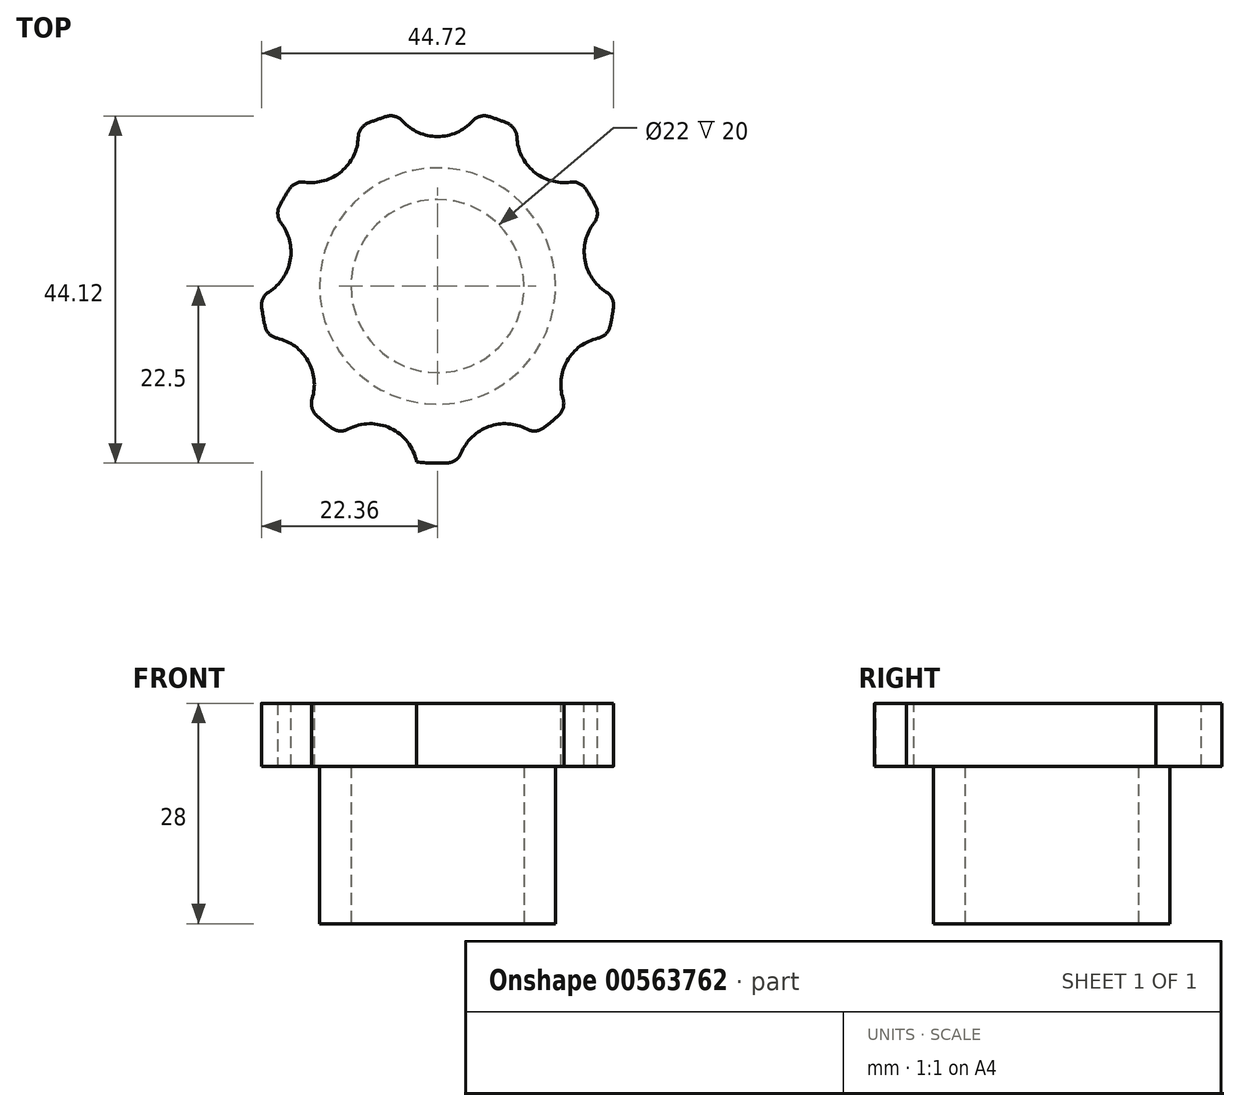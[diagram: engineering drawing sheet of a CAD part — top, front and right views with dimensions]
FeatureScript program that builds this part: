
annotation { "Feature Type Name" : "Feature", "Feature Type Description" : "" }
export const myFeature = defineFeature(function(context is Context, id is Id, definition is map)
    precondition{}
    {
        {
            var Q0;
            Q0=qCreatedBy(makeId("Top.planeOp"),FACE);
            var sketch = newSketch(context, id + "F0", { "sketchPlane" : qUnion([Q0])});
            skCircle(sketch, "E0", {"center": v(0, 0) * mm, "radius": 11 * mm});
            skCircle(sketch, "E1", {"center": v(0, 0) * mm, "radius": 15 * mm});
            skSolve(sketch);
        }
        {
            var Q0;
            Q0=makeQuery(id+"F0.imprint","IMPRINT",FACE,{"disambiguationData":[TD([[makeQuery(id+"F0.imprint","IMPRINT",EDGE,{"derivedFrom":sQuery(id+"F0.wireOp",EDGE,"E0")}),-1.0]])]});
            extrude(context, id + "F1", {"entities" : qUnion([Q0]), "depth" : 20 * mm, "offsetDistance" : 25 * mm});
        }
        {
            var Q0;
            Q0=makeQuery(id+"F1.opExtrude","CAP_FACE",FACE,{"disambiguationData":[OSD([sQuery(id+"F0.wireOp",EDGE,"E0"),sQuery(id+"F0.wireOp",EDGE,"E1")])],"isStart":false});
            var sketch = newSketch(context, id + "F2", { "sketchPlane" : qUnion([Q0])});
            skCircle(sketch, "E2", {"center": v(0, 0) * mm, "radius": 22.5 * mm});
            skSolve(sketch);
        }
        {
            var Q0;
            Q0 = qSketchRegion(id + "F2", true);
            extrude(context, id + "F3", {"entities" : qUnion([Q0]), "operationType" : NewBodyOperationType.ADD, "depth" : 8 * mm, "offsetDistance" : 25 * mm});
        }
        {
            var Q0;
            Q0=makeQuery(id+"F3.opExtrude","CAP_FACE",FACE,{"disambiguationData":[OSD([sQuery(id+"F2.wireOp",EDGE,"E2")])],"isStart":false});
            var sketch = newSketch(context, id + "F4", { "sketchPlane" : qUnion([Q0])});
            skCircle(sketch, "E3", {"center": v(0, 25) * mm, "radius": 6 * mm});
            skCircle(sketch, "E4.1.0", {"center": v(-16.07, 19.15) * mm, "radius": 6 * mm});
            skCircle(sketch, "E4.2.0", {"center": v(-24.62, 4.34) * mm, "radius": 6 * mm});
            skCircle(sketch, "E4.3.0", {"center": v(-21.65, -12.5) * mm, "radius": 6 * mm});
            skCircle(sketch, "E4.4.0", {"center": v(-8.55, -23.5) * mm, "radius": 6 * mm});
            skCircle(sketch, "E4.5.0", {"center": v(8.55, -23.5) * mm, "radius": 6 * mm});
            skCircle(sketch, "E4.6.0", {"center": v(21.65, -12.5) * mm, "radius": 6 * mm});
            skCircle(sketch, "E4.7.0", {"center": v(24.62, 4.34) * mm, "radius": 6 * mm});
            skCircle(sketch, "E4.8.0", {"center": v(16.07, 19.15) * mm, "radius": 6 * mm});
            skPoint(sketch, "E4.center", {"position": v(0, 0) * mm});
            skSolve(sketch);
        }
        {
            var Q0;
            Q0 = qSketchRegion(id + "F4", true);
            extrude(context, id + "F5", {"entities" : qUnion([Q0]), "operationType" : NewBodyOperationType.REMOVE, "oppositeDirection" : true, "depth" : 25 * mm, "offsetDistance" : 25 * mm});
        }
        {
            var Q0;
            Q0=makeQuery(id+"F5.boolean.opBoolean","INTERSECT",EDGE,{"disambiguationData":[OD(0.0)],"derivedFrom":[makeQuery(id+"F3.opExtrude","SWEPT_FACE",FACE,{"disambiguationData":[OSD([sQuery(id+"F2.wireOp",EDGE,"E2")])]}),makeQuery(id+"F5.opExtrude","SWEPT_FACE",FACE,{"disambiguationData":[OSD([sQuery(id+"F4.wireOp",EDGE,"E4.3.0")])]})]});
            var Q1;
            Q1=makeQuery(id+"F5.boolean.opBoolean","INTERSECT",EDGE,{"disambiguationData":[OD(1.0)],"derivedFrom":[makeQuery(id+"F3.opExtrude","SWEPT_FACE",FACE,{"disambiguationData":[OSD([sQuery(id+"F2.wireOp",EDGE,"E2")])]}),makeQuery(id+"F5.opExtrude","SWEPT_FACE",FACE,{"disambiguationData":[OSD([sQuery(id+"F4.wireOp",EDGE,"E4.2.0")])]})]});
            var Q2;
            Q2=makeQuery(id+"F5.boolean.opBoolean","INTERSECT",EDGE,{"disambiguationData":[OD(0.0)],"derivedFrom":[makeQuery(id+"F3.opExtrude","SWEPT_FACE",FACE,{"disambiguationData":[OSD([sQuery(id+"F2.wireOp",EDGE,"E2")])]}),makeQuery(id+"F5.opExtrude","SWEPT_FACE",FACE,{"disambiguationData":[OSD([sQuery(id+"F4.wireOp",EDGE,"E4.2.0")])]})]});
            var Q3;
            Q3=makeQuery(id+"F5.boolean.opBoolean","INTERSECT",EDGE,{"disambiguationData":[OD(1.0)],"derivedFrom":[makeQuery(id+"F3.opExtrude","SWEPT_FACE",FACE,{"disambiguationData":[OSD([sQuery(id+"F2.wireOp",EDGE,"E2")])]}),makeQuery(id+"F5.opExtrude","SWEPT_FACE",FACE,{"disambiguationData":[OSD([sQuery(id+"F4.wireOp",EDGE,"E4.1.0")])]})]});
            var Q4;
            Q4=makeQuery(id+"F5.boolean.opBoolean","INTERSECT",EDGE,{"disambiguationData":[OD(0.0)],"derivedFrom":[makeQuery(id+"F3.opExtrude","SWEPT_FACE",FACE,{"disambiguationData":[OSD([sQuery(id+"F2.wireOp",EDGE,"E2")])]}),makeQuery(id+"F5.opExtrude","SWEPT_FACE",FACE,{"disambiguationData":[OSD([sQuery(id+"F4.wireOp",EDGE,"E4.1.0")])]})]});
            var Q5;
            Q5=makeQuery(id+"F5.boolean.opBoolean","INTERSECT",EDGE,{"disambiguationData":[OD(0.0)],"derivedFrom":[makeQuery(id+"F3.opExtrude","SWEPT_FACE",FACE,{"disambiguationData":[OSD([sQuery(id+"F2.wireOp",EDGE,"E2")])]}),makeQuery(id+"F5.opExtrude","SWEPT_FACE",FACE,{"disambiguationData":[OSD([sQuery(id+"F4.wireOp",EDGE,"E3")])]})]});
            var Q6;
            Q6=makeQuery(id+"F5.boolean.opBoolean","INTERSECT",EDGE,{"disambiguationData":[OD(1.0)],"derivedFrom":[makeQuery(id+"F3.opExtrude","SWEPT_FACE",FACE,{"disambiguationData":[OSD([sQuery(id+"F2.wireOp",EDGE,"E2")])]}),makeQuery(id+"F5.opExtrude","SWEPT_FACE",FACE,{"disambiguationData":[OSD([sQuery(id+"F4.wireOp",EDGE,"E3")])]})]});
            var Q7;
            Q7=makeQuery(id+"F5.boolean.opBoolean","INTERSECT",EDGE,{"disambiguationData":[OD(0.0)],"derivedFrom":[makeQuery(id+"F3.opExtrude","SWEPT_FACE",FACE,{"disambiguationData":[OSD([sQuery(id+"F2.wireOp",EDGE,"E2")])]}),makeQuery(id+"F5.opExtrude","SWEPT_FACE",FACE,{"disambiguationData":[OSD([sQuery(id+"F4.wireOp",EDGE,"E4.8.0")])]})]});
            var Q8;
            Q8=makeQuery(id+"F5.boolean.opBoolean","INTERSECT",EDGE,{"disambiguationData":[OD(1.0)],"derivedFrom":[makeQuery(id+"F3.opExtrude","SWEPT_FACE",FACE,{"disambiguationData":[OSD([sQuery(id+"F2.wireOp",EDGE,"E2")])]}),makeQuery(id+"F5.opExtrude","SWEPT_FACE",FACE,{"disambiguationData":[OSD([sQuery(id+"F4.wireOp",EDGE,"E4.8.0")])]})]});
            var Q9;
            Q9=makeQuery(id+"F5.boolean.opBoolean","INTERSECT",EDGE,{"disambiguationData":[OD(1.0)],"derivedFrom":[makeQuery(id+"F3.opExtrude","SWEPT_FACE",FACE,{"disambiguationData":[OSD([sQuery(id+"F2.wireOp",EDGE,"E2")])]}),makeQuery(id+"F5.opExtrude","SWEPT_FACE",FACE,{"disambiguationData":[OSD([sQuery(id+"F4.wireOp",EDGE,"E4.7.0")])]})]});
            var Q10;
            Q10=makeQuery(id+"F5.boolean.opBoolean","INTERSECT",EDGE,{"disambiguationData":[OD(0.0)],"derivedFrom":[makeQuery(id+"F3.opExtrude","SWEPT_FACE",FACE,{"disambiguationData":[OSD([sQuery(id+"F2.wireOp",EDGE,"E2")])]}),makeQuery(id+"F5.opExtrude","SWEPT_FACE",FACE,{"disambiguationData":[OSD([sQuery(id+"F4.wireOp",EDGE,"E4.7.0")])]})]});
            var Q11;
            Q11=makeQuery(id+"F5.boolean.opBoolean","INTERSECT",EDGE,{"disambiguationData":[OD(1.0)],"derivedFrom":[makeQuery(id+"F3.opExtrude","SWEPT_FACE",FACE,{"disambiguationData":[OSD([sQuery(id+"F2.wireOp",EDGE,"E2")])]}),makeQuery(id+"F5.opExtrude","SWEPT_FACE",FACE,{"disambiguationData":[OSD([sQuery(id+"F4.wireOp",EDGE,"E4.6.0")])]})]});
            var Q12;
            Q12=makeQuery(id+"F5.boolean.opBoolean","INTERSECT",EDGE,{"disambiguationData":[OD(0.0)],"derivedFrom":[makeQuery(id+"F3.opExtrude","SWEPT_FACE",FACE,{"disambiguationData":[OSD([sQuery(id+"F2.wireOp",EDGE,"E2")])]}),makeQuery(id+"F5.opExtrude","SWEPT_FACE",FACE,{"disambiguationData":[OSD([sQuery(id+"F4.wireOp",EDGE,"E4.6.0")])]})]});
            var Q13;
            Q13=makeQuery(id+"F5.boolean.opBoolean","INTERSECT",EDGE,{"disambiguationData":[OD(1.0)],"derivedFrom":[makeQuery(id+"F3.opExtrude","SWEPT_FACE",FACE,{"disambiguationData":[OSD([sQuery(id+"F2.wireOp",EDGE,"E2")])]}),makeQuery(id+"F5.opExtrude","SWEPT_FACE",FACE,{"disambiguationData":[OSD([sQuery(id+"F4.wireOp",EDGE,"E4.5.0")])]})]});
            var Q14;
            Q14=makeQuery(id+"F5.boolean.opBoolean","INTERSECT",EDGE,{"disambiguationData":[OD(0.0)],"derivedFrom":[makeQuery(id+"F3.opExtrude","SWEPT_FACE",FACE,{"disambiguationData":[OSD([sQuery(id+"F2.wireOp",EDGE,"E2")])]}),makeQuery(id+"F5.opExtrude","SWEPT_FACE",FACE,{"disambiguationData":[OSD([sQuery(id+"F4.wireOp",EDGE,"E4.5.0")])]})]});
            var Q15;
            Q15=makeQuery(id+"F5.boolean.opBoolean","INTERSECT",EDGE,{"disambiguationData":[OD(0.0)],"derivedFrom":[makeQuery(id+"F3.opExtrude","SWEPT_FACE",FACE,{"disambiguationData":[OSD([sQuery(id+"F2.wireOp",EDGE,"E2")])]}),makeQuery(id+"F5.opExtrude","SWEPT_FACE",FACE,{"disambiguationData":[OSD([sQuery(id+"F4.wireOp",EDGE,"E4.4.0")])]})]});
            var Q16;
            Q16=makeQuery(id+"F5.boolean.opBoolean","INTERSECT",EDGE,{"disambiguationData":[OD(1.0)],"derivedFrom":[makeQuery(id+"F3.opExtrude","SWEPT_FACE",FACE,{"disambiguationData":[OSD([sQuery(id+"F2.wireOp",EDGE,"E2")])]}),makeQuery(id+"F5.opExtrude","SWEPT_FACE",FACE,{"disambiguationData":[OSD([sQuery(id+"F4.wireOp",EDGE,"E4.3.0")])]})]});
            fillet(context, id + "F6", {"entities" : qUnion([Q0, Q1, Q2, Q3, Q4, Q5, Q6, Q7, Q8, Q9, Q10, Q11, Q12, Q13, Q14, Q15, Q16]), "radius" : 2 * mm, "tangentPropagation" : true, "allowEdgeOverflow" : false});
        }
    });
